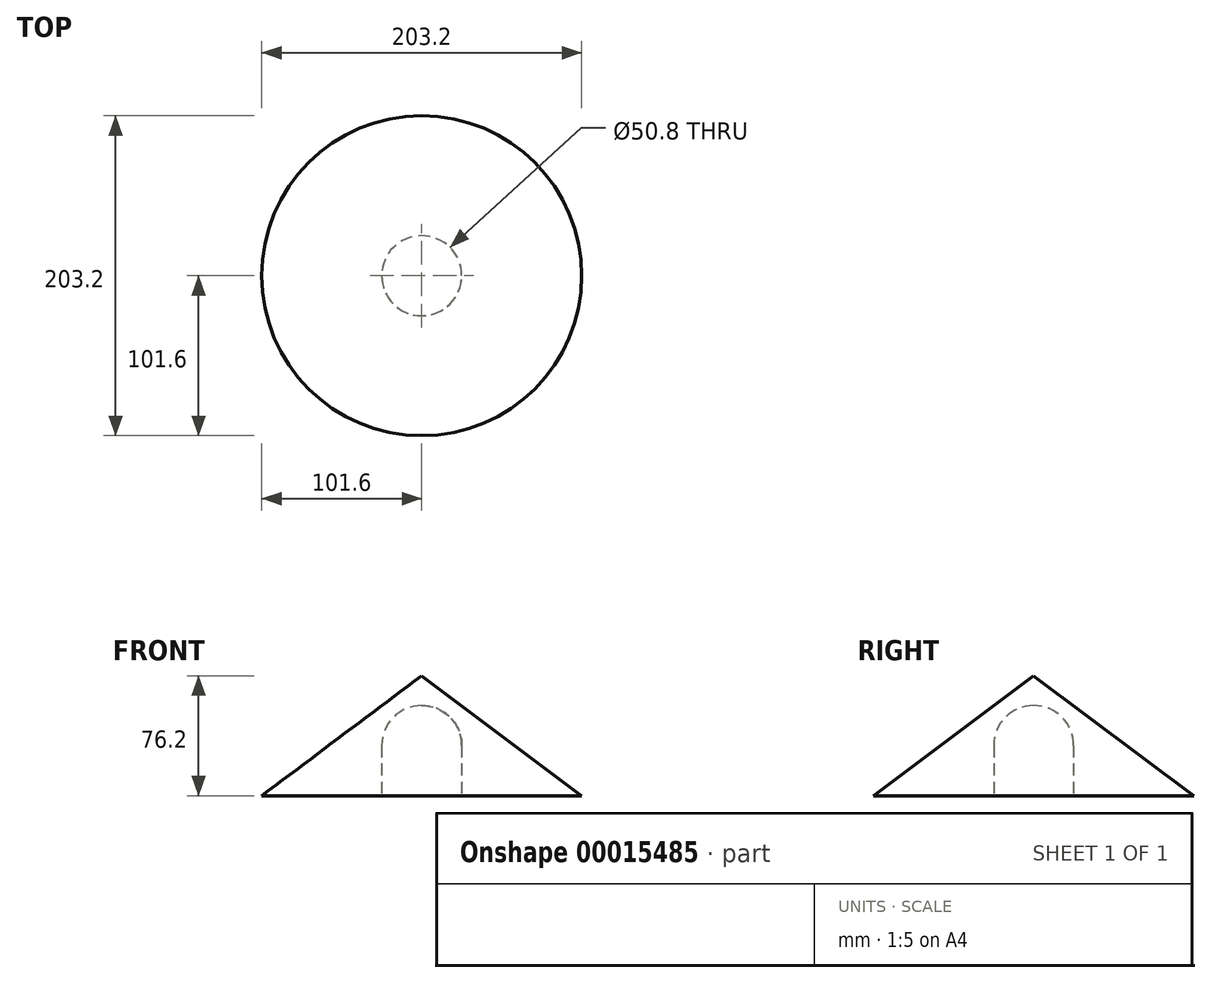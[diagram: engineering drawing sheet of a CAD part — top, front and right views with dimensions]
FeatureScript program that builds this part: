
annotation { "Feature Type Name" : "Feature", "Feature Type Description" : "" }
export const myFeature = defineFeature(function(context is Context, id is Id, definition is map)
    precondition{}
    {
        {
            var Q0;
            Q0=qCreatedBy(makeId("Front.planeOp"),FACE);
            var sketch = newSketch(context, id + "F0", { "sketchPlane" : qUnion([Q0])});
            skLineSegment(sketch, "E0", {"start": v(0, 76.2) * mm, "end": v(101.6, 0) * mm});
            skLineSegment(sketch, "E1", {"start": v(101.6, 0) * mm, "end": v(25.4, 0) * mm});
            skLineSegment(sketch, "E2", {"start": v(25.4, 0) * mm, "end": v(25.4, 31.92) * mm});
            skArc(sketch, "E3", {"start": v(25.4, 31.92) * mm, "mid": v(17.96, 49.88) * mm, "end": v(0, 57.32) * mm});
            skLineSegment(sketch, "E4.trimOffspring", {"start": v(0, 57.32) * mm, "end": v(0, 76.2) * mm});
            skLineSegment(sketch, "E5", {"start": v(0, 57.32) * mm, "end": v(-18.23, 57.32) * mm, "construction": true});
            skSolve(sketch);
        }
        {
            var Q0;
            Q0 = qSketchRegion(id + "F0", true);
            var Q1;
            Q1=sQuery(id+"F0.wireOp",EDGE,"E4.trimOffspring");
            revolve(context, id + "F1", {"entities" : qUnion([Q0]), "axis" : qUnion([Q1]), "revolveType" : RevolveType.FULL});
        }
    });
